# Revit family: NBS_GreshamOfficeFurnitureLtd_OffcChrs_OsanaBench
name_source: partatom
category: Generic Models
units: mm (PartAtom-declared; Revit-internal decimal feet)

## family parameters
Always vertical = Yes
Can host rebar = No
Cut with Voids When Loaded = No
Part Type = Normal
Room Calculation Point = No
Round Connector Dimension = Use Diameter
Shared = No
Work Plane-Based = No

## types (3) — shared parameters
AssetType = Fixed
Category = Pr_40_50_12_57:Office chairs
Color = Brown, Other
Constituents = Wooden base; seat; table top
Description = Soft seating bench
DurationUnit = year
Finish = Stained
FrameColour = Dark Walnut, Natural
FrameFinish = Oak Stained Wood
FrameMaterial = NBS_Gresham_OsanaBench_FrameMaterial
Height = 324 mm  [stored 1.06299 ft]
IfcExportAs = IfcFurnitureType
IfcExportType = Chair
IntegralAccessories = Bench link
LeftSeatMaterial = NBS_Gresham_OsanaBench_SeatMaterial
Length = 593 mm  [stored 1.94554 ft]
ManufacturerName = Gresham Office Furniture Ltd
ManufacturerURL = www.gof.co.uk
Material = Wood
MiddleSeatMaterial = NBS_Gresham_OsanaBench_SeatMaterial
NBSCertification = www.nationalbimlibrary.com/cert/2qax2vgk
RightSeatMaterial = NBS_Gresham_OsanaBench_SeatMaterial
Shape = Square, Rectangle
TableTopMaterial = NBS_Gresham_OsanaBench_FrameMaterial
Uniclass2015Code = Pr_40_50_12_57
Uniclass2015Title = Office chairs
Uniclass2015Version = Products v1.22
Version = 1
WarrantyDescription = Five year
WarrantyDurationUnit = year
zero-valued in all types: Default Elevation, NominalHeight, NominalLength, NominalWidth

## per-type parameters (varying)
| type | BIMObjectName | Name | ShowLeftTop | ShowMiddleTop | ShowRightTop | Width |
| KB3SF3SeaterWoodenBase | NBS_GreshamOfficeFurnitureLtd_OfficeChairs_OsanaBench_KB3SF3SeaterWoodenBase | OfficeChairs_OsanaBench_KB3SF3SeaterWoodenBase_GreshamOfficeFurnitureLtd | Yes | Yes | Yes | 1792 mm  [stored 5.87927 ft] |
| KB2SF2SeaterWoodenBase | NBS_GreshamOfficeFurnitureLtd_OfficeChairs_OsanaBench_KB2SF2SeaterWoodenBase | OfficeChairs_OsanaBench_KB2SF2SeaterWoodenBase_GreshamOfficeFurnitureLtd | Yes | No | Yes | 1192 mm  [stored 3.91076 ft] |
| KB1SF1SeaterWoodenBase | NBS_GreshamOfficeFurnitureLtd_OfficeChairs_OsanaBench_KB1SF1SeaterWoodenBase | OfficeChairs_OsanaBench_KB1SF1SeaterWoodenBase_GreshamOfficeFurnitureLtd | No | Yes | No | 592 mm  [stored 1.94226 ft] |

note: column(s) folded — value = type name in every type: ModelReference

note: [stored X ft] marks values corroborated as IEEE doubles in the binary element streams (Revit-internal decimal feet)

## geometry (parser evidence)
native form markers: Sweep x5
no freeform markers — native parametric forms only
